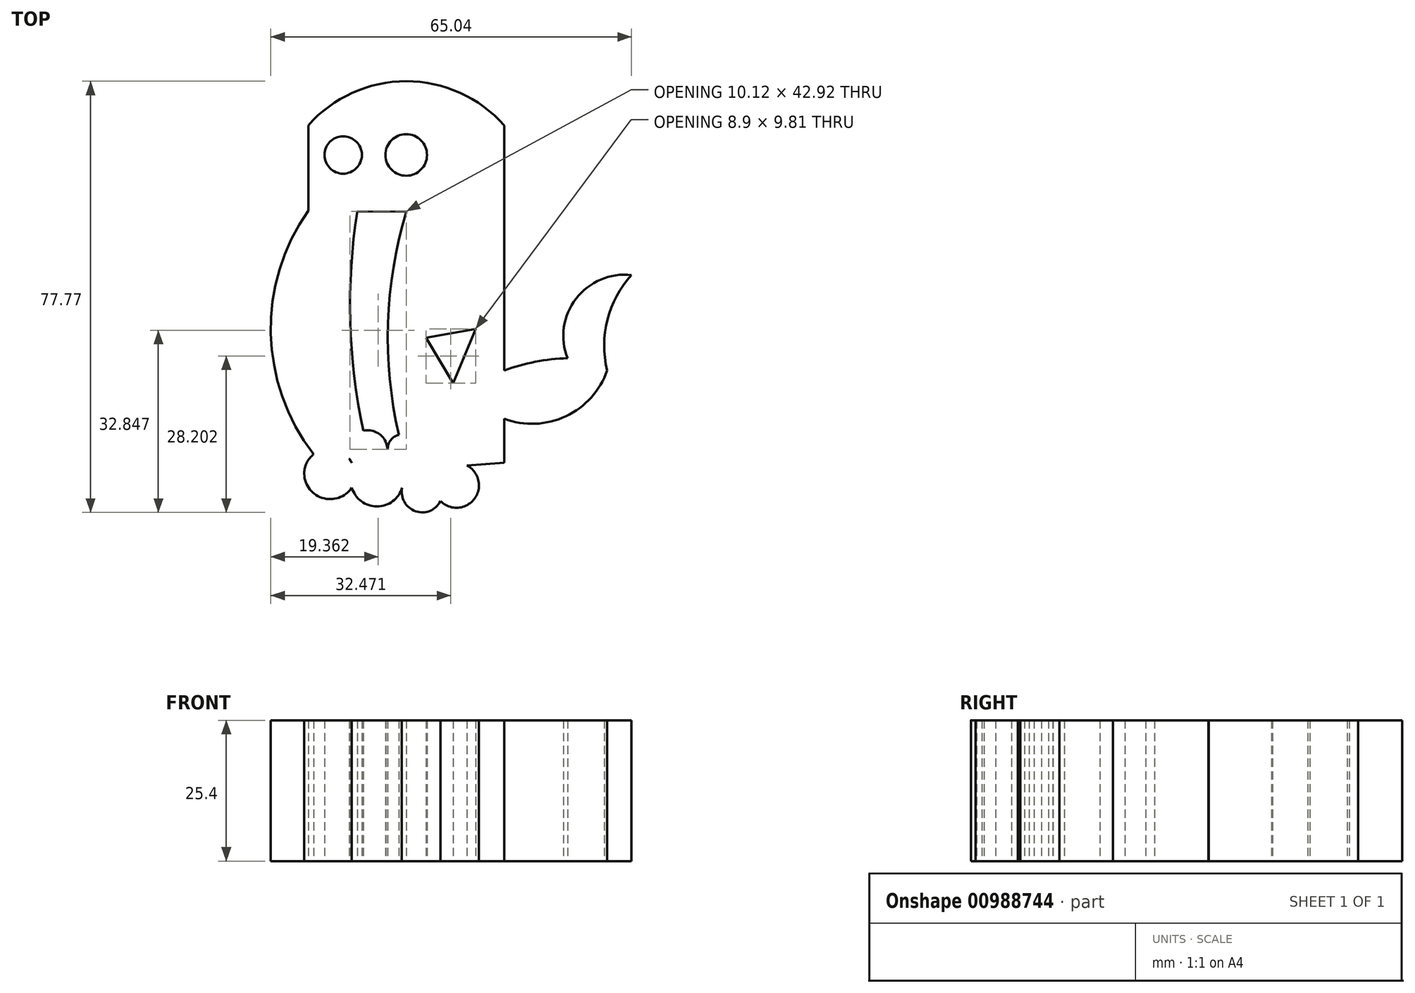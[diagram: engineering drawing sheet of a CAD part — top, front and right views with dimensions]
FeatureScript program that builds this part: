
annotation { "Feature Type Name" : "Feature", "Feature Type Description" : "" }
export const myFeature = defineFeature(function(context is Context, id is Id, definition is map)
    precondition{}
    {
        {
            var Q0;
            Q0=qCreatedBy(makeId("Top.planeOp"),FACE);
            var sketch = newSketch(context, id + "F0", { "sketchPlane" : qUnion([Q0])});
            skLineSegment(sketch, "E0", {"start": v(-11.4, 38.28) * mm, "end": v(-11.4, -5.9) * mm});
            skArc(sketch, "E1", {"start": v(-11.4, 38.28) * mm, "mid": v(-29.07, 46.25) * mm, "end": v(-46.73, 38.28) * mm});
            skLineSegment(sketch, "E2", {"start": v(-46.73, 38.28) * mm, "end": v(-46.73, 22.87) * mm});
            skCircle(sketch, "E3", {"center": v(-40.44, 32.95) * mm, "radius": 3.37 * mm});
            skCircle(sketch, "E4", {"center": v(-29.07, 32.95) * mm, "radius": 3.75 * mm});
            skLineSegment(sketch, "E5", {"start": v(-46.73, 22.87) * mm, "end": v(-29.07, 22.7) * mm});
            skArc(sketch, "E6", {"start": v(-46.73, 22.87) * mm, "mid": v(-53.48, 0.76) * mm, "end": v(-45.75, -21.03) * mm});
            skArc(sketch, "E7", {"start": v(-29.07, 22.7) * mm, "mid": v(-32.35, 2.67) * mm, "end": v(-30.4, -17.54) * mm});
            skLineSegment(sketch, "E8", {"start": v(-16.57, 1.59) * mm, "end": v(-20.58, -8.22) * mm});
            skLineSegment(sketch, "E9", {"start": v(-20.58, -8.22) * mm, "end": v(-25.47, 0) * mm});
            skArc(sketch, "E10", {"start": v(-38.87, -22.6) * mm, "mid": v(-43.78, -20.13) * mm, "end": v(-47.46, -24.2) * mm});
            skArc(sketch, "E11", {"start": v(-32.41, -20.13) * mm, "mid": v(-37.33, -16.94) * mm, "end": v(-38.87, -22.6) * mm});
            skPoint(sketch, "E11.startSnap0", {"position": v(-43.78, -20.13) * mm});
            skArc(sketch, "E12", {"start": v(-27.2, -19.7) * mm, "mid": v(-30.01, -17.47) * mm, "end": v(-32.41, -20.13) * mm});
            skArc(sketch, "E13", {"start": v(-47.46, -24.2) * mm, "mid": v(-44.25, -28.9) * mm, "end": v(-38.87, -27.06) * mm});
            skArc(sketch, "E14", {"start": v(-20, -22.6) * mm, "mid": v(-22.82, -19.18) * mm, "end": v(-27.2, -19.7) * mm});
            skArc(sketch, "E15", {"start": v(-38.87, -27.06) * mm, "mid": v(-34.33, -30.46) * mm, "end": v(-29.8, -27.06) * mm});
            skArc(sketch, "E16", {"start": v(-22.88, -29.5) * mm, "mid": v(-16.28, -28.2) * mm, "end": v(-20, -22.6) * mm});
            skArc(sketch, "E17", {"start": v(-29.8, -27.06) * mm, "mid": v(-27.4, -31.3) * mm, "end": v(-22.88, -29.5) * mm});
            skArc(sketch, "E18", {"start": v(-33.5, 22.74) * mm, "mid": v(-35.4, 1.24) * mm, "end": v(-32.41, -20.13) * mm});
            skArc(sketch, "E19", {"start": v(-37.9, 22.79) * mm, "mid": v(-39.1, 1.23) * mm, "end": v(-36.03, -20.13) * mm});
            skArc(sketch, "E20", {"start": v(-43.78, 22.59) * mm, "mid": v(-48.25, 1.02) * mm, "end": v(-42.1, -20.13) * mm});
            skArc(sketch, "E21", {"start": v(-29.07, 49.07) * mm, "mid": v(-32.98, 48.9) * mm, "end": v(-34.95, 45.5) * mm});
            skPoint(sketch, "E21.startSnap0", {"position": v(-29.07, 46.25) * mm});
            skArc(sketch, "E22", {"start": v(-17.41, 46.25) * mm, "mid": v(-22.44, 50.97) * mm, "end": v(-29.07, 49.07) * mm});
            skArc(sketch, "E23", {"start": v(-14.94, 41.55) * mm, "mid": v(-15.55, 44.2) * mm, "end": v(-17.34, 46.25) * mm});
            skLineSegment(sketch, "E24", {"start": v(-11.4, -22.6) * mm, "end": v(-18.16, -23.04) * mm});
            skArc(sketch, "E25", {"start": v(-11.4, -14.65) * mm, "mid": v(-0.29, -14.18) * mm, "end": v(7.16, -5.9) * mm});
            skArc(sketch, "E26", {"start": v(12.49, 12.24) * mm, "mid": v(7.37, 3.89) * mm, "end": v(7.16, -5.9) * mm});
            skArc(sketch, "E27", {"start": v(0, -3.73) * mm, "mid": v(-5.8, -4.36) * mm, "end": v(-11.4, -5.9) * mm});
            skArc(sketch, "E28", {"start": v(11.55, 11.28) * mm, "mid": v(1.54, 7.03) * mm, "end": v(0, -3.73) * mm});
            skPoint(sketch, "E29.start.orphan", {"position": v(-17.34, 43.12) * mm});
            skPoint(sketch, "E30.orphan", {"position": v(-32.41, 41.6) * mm});
            skLineSegment(sketch, "E31.trimOffspring", {"start": v(-11.4, -14.65) * mm, "end": v(-11.4, -22.6) * mm});
            skPoint(sketch, "E32.orphan", {"position": v(-29.07, -22.6) * mm});
            skPoint(sketch, "E33.orphan", {"position": v(-44.47, -22.6) * mm});
            skLineSegment(sketch, "E34", {"start": v(-25.47, 0) * mm, "end": v(-16.57, 1.59) * mm});
            skSolve(sketch);
        }
        {
            var Q0;
            Q0 = qSketchRegion(id + "F0", true);
            extrude(context, id + "F1", {"entities" : qUnion([Q0]), "depth" : 25.4 * mm, "offsetDistance" : 25.4 * mm});
        }
        {
            var Q0;
            Q0=sQuery(id+"F0.wireOp",EDGE,"E4");
            extrude(context, id + "F2", {"bodyType" : ToolBodyType.SURFACE, "surfaceEntities" : qUnion([Q0]), "depth" : 50.8 * mm, "offsetDistance" : 25.4 * mm});
        }
    });
